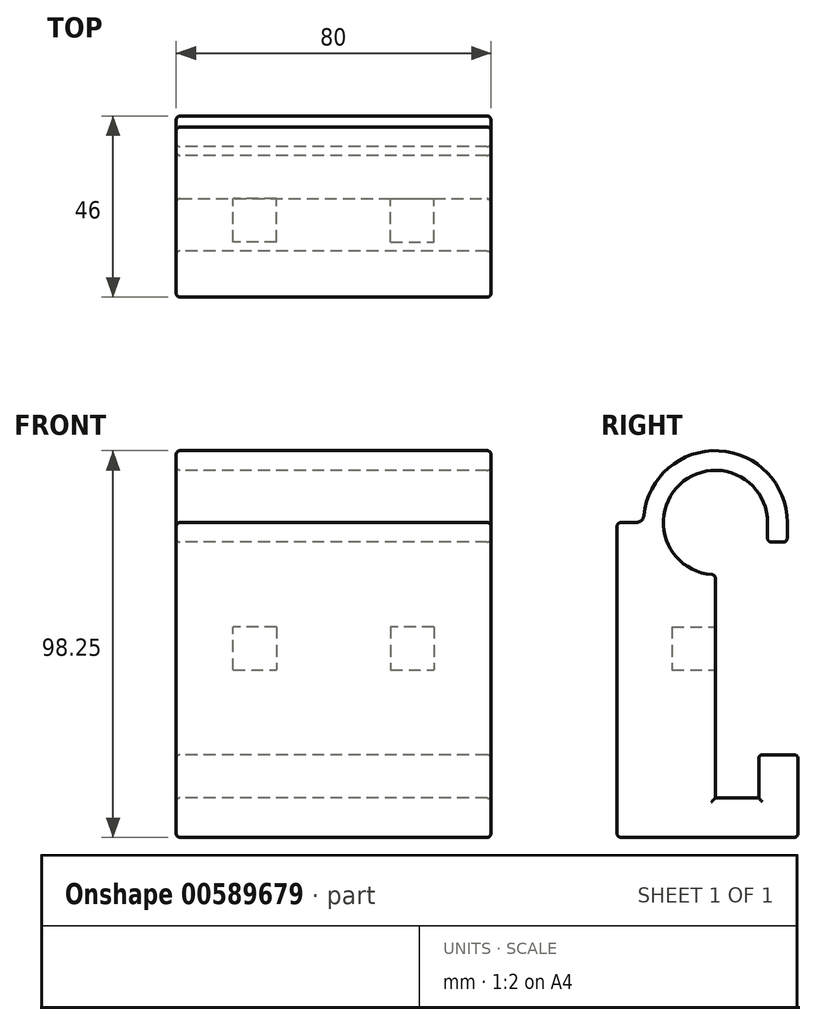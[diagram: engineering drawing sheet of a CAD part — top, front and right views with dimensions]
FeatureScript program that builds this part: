
annotation { "Feature Type Name" : "Feature", "Feature Type Description" : "" }
export const myFeature = defineFeature(function(context is Context, id is Id, definition is map)
    precondition{}
    {
        {
            var Q0;
            Q0=qCreatedBy(makeId("Right.planeOp"),FACE);
            var sketch = newSketch(context, id + "F0", { "sketchPlane" : qUnion([Q0])});
            skCircle(sketch, "E0", {"center": v(0, 0) * mm, "radius": 18.25 * mm});
            skLineSegment(sketch, "E1", {"start": v(-25, 0) * mm, "end": v(-25, -80) * mm});
            skLineSegment(sketch, "E2", {"start": v(-25, -80) * mm, "end": v(21, -80) * mm});
            skLineSegment(sketch, "E3", {"start": v(21, -80) * mm, "end": v(21, -59) * mm});
            skLineSegment(sketch, "E4", {"start": v(21, -59) * mm, "end": v(11, -59) * mm});
            skLineSegment(sketch, "E5", {"start": v(11, -59) * mm, "end": v(11, -70) * mm});
            skLineSegment(sketch, "E6", {"start": v(11, -70) * mm, "end": v(0, -70) * mm});
            skLineSegment(sketch, "E7", {"start": v(0, -70) * mm, "end": v(0, -18.25) * mm});
            skLineSegment(sketch, "E8", {"start": v(-25, 0) * mm, "end": v(0, 0) * mm});
            skLineSegment(sketch, "E9", {"start": v(0, 0) * mm, "end": v(0, -18.25) * mm});
            skCircle(sketch, "E10", {"center": v(0, 0) * mm, "radius": 13.25 * mm});
            skLineSegment(sketch, "E11", {"start": v(0, 0) * mm, "end": v(18.25, 0) * mm});
            skLineSegment(sketch, "E12", {"start": v(13.25, 0) * mm, "end": v(13.25, -5) * mm});
            skLineSegment(sketch, "E13", {"start": v(13.25, -5) * mm, "end": v(18.25, -5) * mm});
            skLineSegment(sketch, "E14", {"start": v(18.25, -5) * mm, "end": v(18.25, 0) * mm});
            skSolve(sketch);
        }
        {
            var Q0;
            {var subQ0=sQuery(id+"F0.wireOp",EDGE,"E1");Q0=makeQuery(id+"F0.imprint","IMPRINT",FACE,{"disambiguationData":[TD([[makeQuery(id+"F0.imprint","IMPRINT",EDGE,{"derivedFrom":subQ0}),1.0]])]});}
            var Q1;
            {var subQ1=sQuery(id+"F0.wireOp",EDGE,"E0");var subQ3=sQuery(id+"F0.wireOp",EDGE,"E8");var subQ4=makeQuery(id+"F0.imprint","INTERSECT",VERTEX,{"derivedFrom":[subQ1,subQ3]});Q1=makeQuery(id+"F0.imprint","IMPRINT",FACE,{"disambiguationData":[TD([[makeQuery(id+"F0.imprint","IMPRINT",EDGE,{"disambiguationData":[TD([[subQ4,-1.0]])],"derivedFrom":subQ3}),-1.0]])]});}
            var Q2;
            {var subQ4=sQuery(id+"F0.wireOp",EDGE,"E13");Q2=makeQuery(id+"F0.imprint","IMPRINT",FACE,{"disambiguationData":[TD([[makeQuery(id+"F0.imprint","IMPRINT",EDGE,{"derivedFrom":subQ4}),1.0]])]});}
            var Q3;
            {var subQ1=sQuery(id+"F0.wireOp",EDGE,"E0");var subQ3=sQuery(id+"F0.wireOp",EDGE,"E12");var subQ4=makeQuery(id+"F0.imprint","INTERSECT",VERTEX,{"derivedFrom":[subQ1,subQ3]});Q3=makeQuery(id+"F0.imprint","IMPRINT",FACE,{"disambiguationData":[TD([[makeQuery(id+"F0.imprint","IMPRINT",EDGE,{"disambiguationData":[TD([[subQ4,-1.0]])],"derivedFrom":subQ1}),1.0]])]});}
            var Q4;
            {var subQ1=sQuery(id+"F0.wireOp",EDGE,"E0");var subQ3=sQuery(id+"F0.wireOp",EDGE,"E8");var subQ4=makeQuery(id+"F0.imprint","INTERSECT",VERTEX,{"derivedFrom":[subQ1,subQ3]});Q4=makeQuery(id+"F0.imprint","IMPRINT",FACE,{"disambiguationData":[TD([[makeQuery(id+"F0.imprint","IMPRINT",EDGE,{"disambiguationData":[TD([[subQ4,-1.0]])],"derivedFrom":subQ3}),1.0]])]});}
            extrude(context, id + "F1", {"entities" : qUnion([Q0, Q1, Q2, Q3, Q4]), "endBound" : BoundingType.SYMMETRIC, "depth" : 80 * mm, "offsetDistance" : 25 * mm});
        }
        {
            var Q0;
            Q0=makeQuery(id+"F1.opExtrude","SWEPT_FACE",FACE,{"disambiguationData":[OSD([sQuery(id+"F0.wireOp",EDGE,"E7"),sQuery(id+"F0.wireOp",EDGE,"E9")])]});
            var sketch = newSketch(context, id + "F2", { "sketchPlane" : qUnion([Q0])});
            skLineSegment(sketch, "E15.0", {"start": v(-40, -5) * mm, "end": v(40, -5) * mm});
            skLineSegment(sketch, "E15.1", {"start": v(40, -70) * mm, "end": v(40, -13.25) * mm});
            skLineSegment(sketch, "E15.2", {"start": v(-40, -13.25) * mm, "end": v(40, -13.25) * mm});
            skLineSegment(sketch, "E15.3", {"start": v(-40, -70) * mm, "end": v(-40, -13.25) * mm});
            skLineSegment(sketch, "E15.4", {"start": v(-40, -59) * mm, "end": v(40, -59) * mm});
            skLineSegment(sketch, "E15.5", {"start": v(-40, -80) * mm, "end": v(40, -80) * mm});
            skLineSegment(sketch, "E16", {"start": v(0, -5) * mm, "end": v(0, -59) * mm});
            skLineSegment(sketch, "E17", {"start": v(0, -32) * mm, "end": v(-40, -32) * mm});
            skLineSegment(sketch, "E18", {"start": v(-20, -32) * mm, "end": v(-20, -5) * mm});
            skLineSegment(sketch, "E19", {"start": v(-20, -26.5) * mm, "end": v(-25.5, -26.5) * mm});
            skLineSegment(sketch, "E20", {"start": v(-25.5, -26.5) * mm, "end": v(-25.5, -32) * mm});
            skLineSegment(sketch, "E21.MirrorCS", {"start": v(-20, -37.5) * mm, "end": v(-25.5, -37.5) * mm});
            skLineSegment(sketch, "E22.MirrorCS", {"start": v(-25.5, -37.5) * mm, "end": v(-25.5, -32) * mm});
            skLineSegment(sketch, "E23.MirrorCS", {"start": v(-20, -37.5) * mm, "end": v(-14.5, -37.5) * mm});
            skLineSegment(sketch, "E24.MirrorCS", {"start": v(-14.5, -37.5) * mm, "end": v(-14.5, -32) * mm});
            skLineSegment(sketch, "E25.MirrorCS", {"start": v(-20, -26.5) * mm, "end": v(-14.5, -26.5) * mm});
            skLineSegment(sketch, "E26.MirrorCS", {"start": v(-14.5, -26.5) * mm, "end": v(-14.5, -32) * mm});
            skLineSegment(sketch, "E27.MirrorCS", {"start": v(20, -26.5) * mm, "end": v(14.5, -26.5) * mm});
            skLineSegment(sketch, "E28.MirrorCS", {"start": v(14.5, -26.5) * mm, "end": v(14.5, -32) * mm});
            skLineSegment(sketch, "E29.MirrorCS", {"start": v(14.5, -37.5) * mm, "end": v(14.5, -32) * mm});
            skLineSegment(sketch, "E30.MirrorCS", {"start": v(20, -37.5) * mm, "end": v(14.5, -37.5) * mm});
            skLineSegment(sketch, "E31.MirrorCS", {"start": v(20, -37.5) * mm, "end": v(25.5, -37.5) * mm});
            skLineSegment(sketch, "E32.MirrorCS", {"start": v(25.5, -37.5) * mm, "end": v(25.5, -32) * mm});
            skLineSegment(sketch, "E33.MirrorCS", {"start": v(20, -26.5) * mm, "end": v(25.5, -26.5) * mm});
            skLineSegment(sketch, "E34.MirrorCS", {"start": v(25.5, -26.5) * mm, "end": v(25.5, -32) * mm});
            skSolve(sketch);
        }
        {
            var Q0;
            {var subQ4=sQuery(id+"F2.wireOp",EDGE,"E25.MirrorCS");Q0=makeQuery(id+"F2.imprint","IMPRINT",FACE,{"disambiguationData":[TD([[makeQuery(id+"F2.imprint","IMPRINT",EDGE,{"derivedFrom":subQ4}),-1.0]])]});}
            var Q1;
            {var subQ4=sQuery(id+"F2.wireOp",EDGE,"E19");Q1=makeQuery(id+"F2.imprint","IMPRINT",FACE,{"disambiguationData":[TD([[makeQuery(id+"F2.imprint","IMPRINT",EDGE,{"derivedFrom":subQ4}),1.0]])]});}
            var Q2;
            Q2=makeQuery(id+"F2.imprint","IMPRINT",FACE,{"disambiguationData":[TD([[makeQuery(id+"F2.imprint","IMPRINT",EDGE,{"derivedFrom":sQuery(id+"F2.wireOp",EDGE,"E21.MirrorCS")}),-1.0]])]});
            var Q3;
            Q3=makeQuery(id+"F2.imprint","IMPRINT",FACE,{"disambiguationData":[TD([[makeQuery(id+"F2.imprint","IMPRINT",EDGE,{"derivedFrom":sQuery(id+"F2.wireOp",EDGE,"E27.MirrorCS")}),1.0]])]});
            extrude(context, id + "F3", {"entities" : qUnion([Q0, Q1, Q2, Q3]), "operationType" : NewBodyOperationType.REMOVE, "oppositeDirection" : true, "depth" : 11 * mm, "offsetDistance" : 25 * mm});
        }
        {
            var Q0;
            Q0=makeQuery(id+"F1.opExtrude","SWEPT_EDGE",EDGE,{"disambiguationData":[OSD([sQuery(id+"F0.wireOp",EDGE,"E0"),sQuery(id+"F0.wireOp",EDGE,"E8")])]});
            fillet(context, id + "F4", {"entities" : qUnion([Q0]), "radius" : 2 * mm, "tangentPropagation" : true, "allowEdgeOverflow" : false});
        }
        {
            var Q0;
            Q0=makeQuery(id+"F1.opExtrude","CAP_FACE",FACE,{"disambiguationData":[OSD([sQuery(id+"F0.wireOp",EDGE,"E0"),sQuery(id+"F0.wireOp",EDGE,"E1"),sQuery(id+"F0.wireOp",EDGE,"E2"),sQuery(id+"F0.wireOp",EDGE,"E3"),sQuery(id+"F0.wireOp",EDGE,"E4"),sQuery(id+"F0.wireOp",EDGE,"E5"),sQuery(id+"F0.wireOp",EDGE,"E6"),sQuery(id+"F0.wireOp",EDGE,"E7"),sQuery(id+"F0.wireOp",EDGE,"E8"),sQuery(id+"F0.wireOp",EDGE,"E9"),sQuery(id+"F0.wireOp",EDGE,"E10"),sQuery(id+"F0.wireOp",EDGE,"E12"),sQuery(id+"F0.wireOp",EDGE,"E13"),sQuery(id+"F0.wireOp",EDGE,"E14")])],"isStart":true});
            var Q1;
            Q1=makeQuery(id+"F1.opExtrude","SWEPT_FACE",FACE,{"disambiguationData":[OSD([sQuery(id+"F0.wireOp",EDGE,"E1")])]});
            var Q2;
            Q2=makeQuery(id+"F1.opExtrude","CAP_FACE",FACE,{"disambiguationData":[OSD([sQuery(id+"F0.wireOp",EDGE,"E0"),sQuery(id+"F0.wireOp",EDGE,"E1"),sQuery(id+"F0.wireOp",EDGE,"E2"),sQuery(id+"F0.wireOp",EDGE,"E3"),sQuery(id+"F0.wireOp",EDGE,"E4"),sQuery(id+"F0.wireOp",EDGE,"E5"),sQuery(id+"F0.wireOp",EDGE,"E6"),sQuery(id+"F0.wireOp",EDGE,"E7"),sQuery(id+"F0.wireOp",EDGE,"E8"),sQuery(id+"F0.wireOp",EDGE,"E9"),sQuery(id+"F0.wireOp",EDGE,"E10"),sQuery(id+"F0.wireOp",EDGE,"E12"),sQuery(id+"F0.wireOp",EDGE,"E13"),sQuery(id+"F0.wireOp",EDGE,"E14")])],"isStart":false});
            var Q3;
            Q3=makeQuery(id+"F1.opExtrude","SWEPT_FACE",FACE,{"disambiguationData":[OSD([sQuery(id+"F0.wireOp",EDGE,"E2")])]});
            var Q4;
            Q4=makeQuery(id+"F1.opExtrude","SWEPT_FACE",FACE,{"disambiguationData":[OSD([sQuery(id+"F0.wireOp",EDGE,"E3")])]});
            var Q5;
            Q5=makeQuery(id+"F1.opExtrude","SWEPT_FACE",FACE,{"disambiguationData":[OSD([sQuery(id+"F0.wireOp",EDGE,"E4")])]});
            var Q6;
            Q6=makeQuery(id+"F1.opExtrude","SWEPT_EDGE",EDGE,{"disambiguationData":[OSD([sQuery(id+"F0.wireOp",EDGE,"E13"),sQuery(id+"F0.wireOp",EDGE,"E14")])]});
            var Q7;
            Q7=makeQuery(id+"F1.opExtrude","SWEPT_EDGE",EDGE,{"disambiguationData":[OSD([sQuery(id+"F0.wireOp",EDGE,"E12"),sQuery(id+"F0.wireOp",EDGE,"E13")])]});
            var Q8;
            Q8=makeQuery(id+"F1.opExtrude","SWEPT_EDGE",EDGE,{"disambiguationData":[OSD([sQuery(id+"F0.wireOp",EDGE,"E9"),sQuery(id+"F0.wireOp",EDGE,"E10")])]});
            var Q9;
            Q9=makeQuery(id+"F3.boolean.opBoolean","COPY",EDGE,{"derivedFrom":makeQuery(id+"F3.opExtrude","CAP_EDGE",EDGE,{"disambiguationData":[OSD([sQuery(id+"F2.wireOp",EDGE,"E20"),sQuery(id+"F2.wireOp",EDGE,"E22.MirrorCS")])],"isStart":true})});
            var Q10;
            Q10=makeQuery(id+"F3.boolean.opBoolean","COPY",EDGE,{"derivedFrom":makeQuery(id+"F3.opExtrude","CAP_EDGE",EDGE,{"disambiguationData":[OSD([sQuery(id+"F2.wireOp",EDGE,"E19"),sQuery(id+"F2.wireOp",EDGE,"E25.MirrorCS")])],"isStart":true})});
            var Q11;
            Q11=makeQuery(id+"F3.boolean.opBoolean","COPY",EDGE,{"derivedFrom":makeQuery(id+"F3.opExtrude","CAP_EDGE",EDGE,{"disambiguationData":[OSD([sQuery(id+"F2.wireOp",EDGE,"E24.MirrorCS"),sQuery(id+"F2.wireOp",EDGE,"E26.MirrorCS")])],"isStart":true})});
            var Q12;
            Q12=makeQuery(id+"F3.boolean.opBoolean","COPY",EDGE,{"derivedFrom":makeQuery(id+"F3.opExtrude","CAP_EDGE",EDGE,{"disambiguationData":[OSD([sQuery(id+"F2.wireOp",EDGE,"E21.MirrorCS"),sQuery(id+"F2.wireOp",EDGE,"E23.MirrorCS")])],"isStart":true})});
            var Q13;
            Q13=makeQuery(id+"F3.boolean.opBoolean","COPY",EDGE,{"derivedFrom":makeQuery(id+"F3.opExtrude","CAP_EDGE",EDGE,{"disambiguationData":[OSD([sQuery(id+"F2.wireOp",EDGE,"E28.MirrorCS"),sQuery(id+"F2.wireOp",EDGE,"E29.MirrorCS")])],"isStart":true})});
            var Q14;
            Q14=makeQuery(id+"F3.boolean.opBoolean","COPY",EDGE,{"derivedFrom":makeQuery(id+"F3.opExtrude","CAP_EDGE",EDGE,{"disambiguationData":[OSD([sQuery(id+"F2.wireOp",EDGE,"E27.MirrorCS"),sQuery(id+"F2.wireOp",EDGE,"E33.MirrorCS")])],"isStart":true})});
            var Q15;
            Q15=makeQuery(id+"F3.boolean.opBoolean","COPY",EDGE,{"derivedFrom":makeQuery(id+"F3.opExtrude","CAP_EDGE",EDGE,{"disambiguationData":[OSD([sQuery(id+"F2.wireOp",EDGE,"E32.MirrorCS"),sQuery(id+"F2.wireOp",EDGE,"E34.MirrorCS")])],"isStart":true})});
            var Q16;
            Q16=makeQuery(id+"F3.boolean.opBoolean","COPY",EDGE,{"derivedFrom":makeQuery(id+"F3.opExtrude","CAP_EDGE",EDGE,{"disambiguationData":[OSD([sQuery(id+"F2.wireOp",EDGE,"E30.MirrorCS"),sQuery(id+"F2.wireOp",EDGE,"E31.MirrorCS")])],"isStart":true})});
            fillet(context, id + "F5", {"entities" : qUnion([Q0, Q1, Q2, Q3, Q4, Q5, Q6, Q7, Q8, Q9, Q10, Q11, Q12, Q13, Q14, Q15, Q16]), "radius" : 1 * mm, "tangentPropagation" : true, "allowEdgeOverflow" : false});
        }
    });
